# Revit family: IS_Ceraplan_B3697_BIM_GB
name_source: partatom
category: Plumbing Fixtures
revit_build: Autodesk Revit MEP 2014 (Build: 20130308_1515(x64)
units: mm (PartAtom-declared; Revit-internal decimal feet)

## types (1)
- B3697AA - Ceraplan Bath Shower Mixer Exposed Wall Mounted Single Lever
    Accessories = www.idealspec.co.uk
    AreaUnits = millimeters
    Assembly Code = C1030200
    AssetType = Fixed
    BIMObjectName = ISI_IdealStandard_BathTaps_Ceraplan_B3697AA
    BREEAMApproved = No
    BarCode = 3800019242197
    Brand = Ideal Standard
    CWFU = 0
    Color = Chrome
    ConnectionType = Plumbing
    Cost = 0 $
    Default Elevation = 0 mm  [stored 0 ft]
    Description = Ceraplan bath shower mixer exposed wall mounted single lever
    DurationUnit = year
    ECA = No
    ExpectedLife = 30
    FaucetFunction = MIXED
    FaucetOperation = LEVERHANDLE
    FaucetType = OTHER
    Features = Bath shower mixer exposed wall mounted single lever
    Finish = Chrome
    FlowRate = 11L/min @ 3Bar
    HWFU = 0
    Help = www.idealspec.co.uk/contact-us.html
    IfcExportAs = IfcValveType
    IfcExportType = FAUCET
    InstallationInstructions = www.idealspec.co.uk/resources.html
    LinearUnits = millimeters
    ManufacturerURL = www.idealspec.co.uk
    Material = Brass
    Model = B3697AA
    ModelNumber = B3697AA
    ModelReference = Ceraplan bath shower mixer exposed wall mounted single lever
    NBSDescription = Water supply fittings for baths
    NBSReference = 45-35-70/315
    Name = BathTaps_Ceraplan_B3697AA_IdealStandard
    NettWeight = 2 Kg
    NominalHeight = 121 mm
    NominalLength = 182 mm
    NominalWidth = 220 mm
    ProductInformation = www.idealspec.co.uk/assets/datasheet/B3697AA
    Shape = Sculptured
    Size = 122 x 182 x 220 mm
    Space = Internal
    SpareParts = www.fastpart-spares.co.uk
    TMV3 = No
    TestPressure = 10 Bar
    URL = www.idealspec.co.uk
    Version = 2
    VolumeUnits = Litres
    WFU = 0
    WRAS = No
    WarrantyDescription = Manufacturers Warranty
    WarrantyDurationParts = 5
    WarrantyDurationUnit = year
    WaterEfficientProduct = No
    WorkingPressure = 3 Bar

note: [stored X ft] marks values corroborated as IEEE doubles in the binary element streams (Revit-internal decimal feet)

## geometry (parser evidence)
native form markers: Sweep x3
no freeform markers — native parametric forms only
